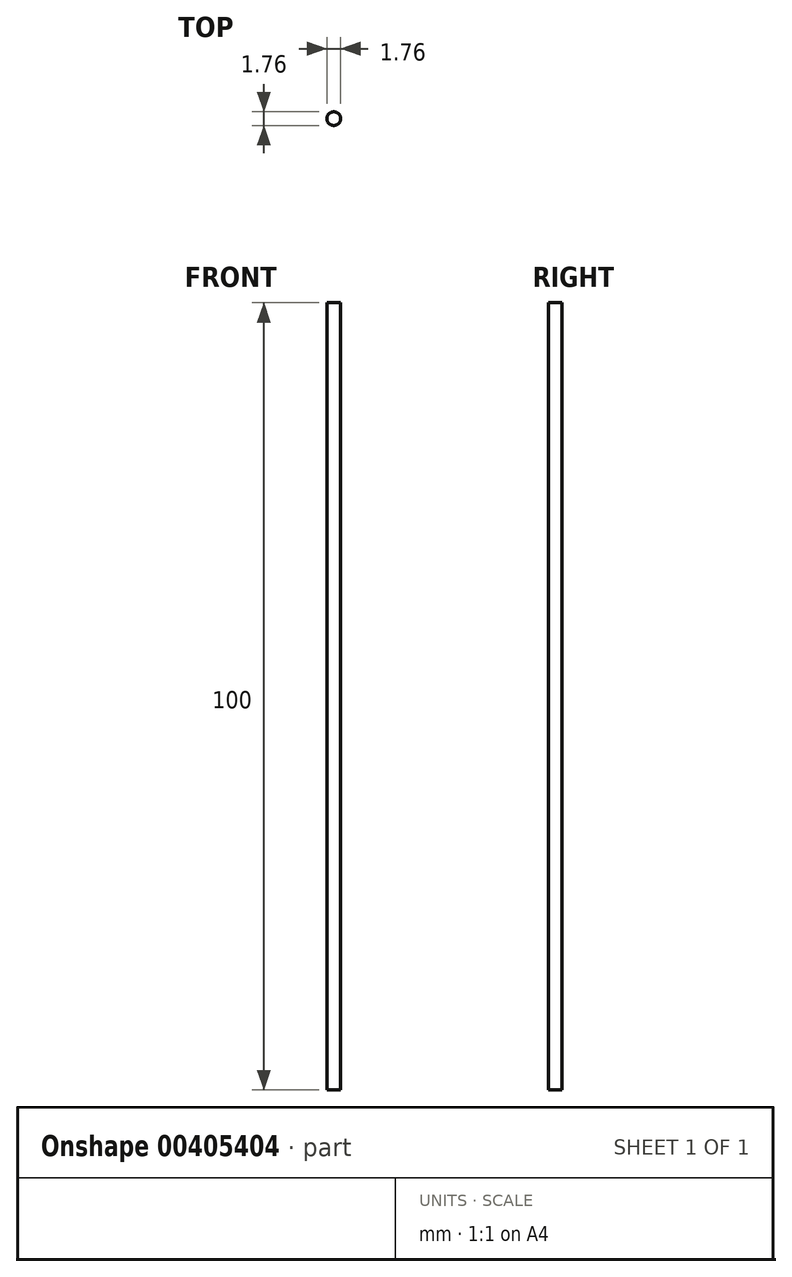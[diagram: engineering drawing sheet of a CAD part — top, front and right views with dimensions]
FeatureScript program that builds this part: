
annotation { "Feature Type Name" : "Feature", "Feature Type Description" : "" }
export const myFeature = defineFeature(function(context is Context, id is Id, definition is map)
    precondition{}
    {
        {
            var Q0;
            Q0=qCreatedBy(makeId("Top.planeOp"),FACE);
            var sketch = newSketch(context, id + "F0", { "sketchPlane" : qUnion([Q0])});
            skCircle(sketch, "E0", {"center": v(0, 0) * mm, "radius": 0.88 * mm});
            skSolve(sketch);
        }
        {
            var Q0;
            Q0=qSketchRegion(id+"F0",true);
            extrude(context, id + "F1", {"entities" : qUnion([Q0]), "depth" : 100 * mm});
        }
    });
